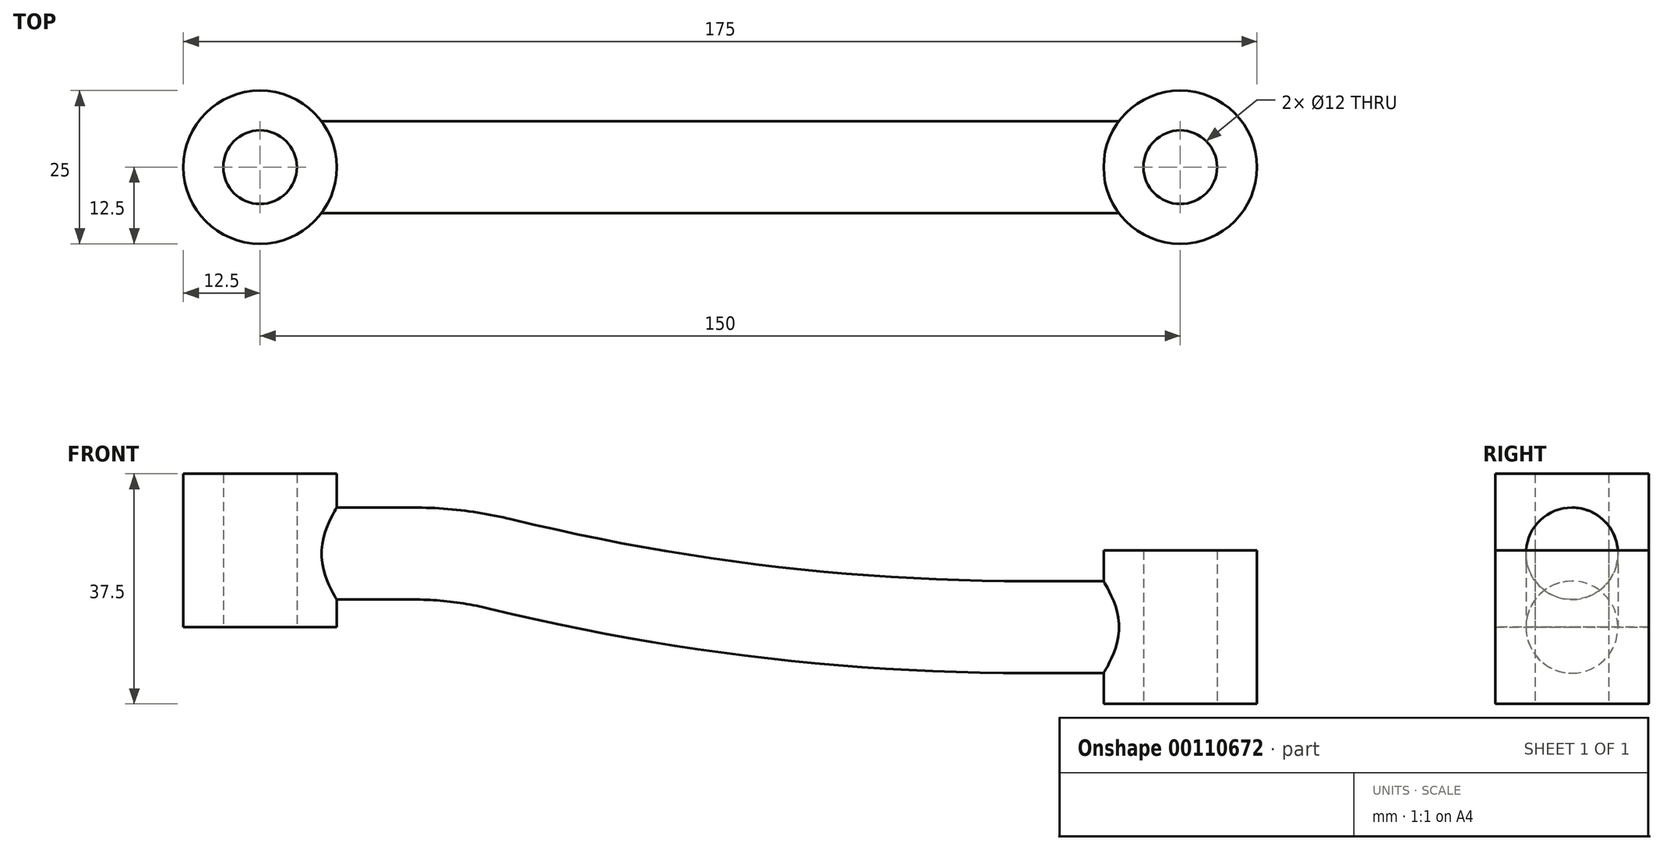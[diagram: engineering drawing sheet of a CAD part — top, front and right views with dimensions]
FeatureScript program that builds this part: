
annotation { "Feature Type Name" : "Feature", "Feature Type Description" : "" }
export const myFeature = defineFeature(function(context is Context, id is Id, definition is map)
    precondition{}
    {
        {
            var Q0;
            Q0=qCreatedBy(makeId("Top.planeOp"),FACE);
            var sketch = newSketch(context, id + "F0", { "sketchPlane" : qUnion([Q0])});
            skCircle(sketch, "E0", {"center": v(0, 0) * mm, "radius": 12.5 * mm});
            skCircle(sketch, "E1", {"center": v(0, 0) * mm, "radius": 6 * mm});
            skCircle(sketch, "E2", {"center": v(150, 0) * mm, "radius": 12.5 * mm});
            skCircle(sketch, "E3", {"center": v(150, 0) * mm, "radius": 6 * mm});
            skLineSegment(sketch, "E4", {"start": v(150, 0) * mm, "end": v(150, 287.37) * mm, "construction": true});
            skSolve(sketch);
        }
        {
            var Q0;
            Q0=makeQuery(id+"F0.imprint","IMPRINT",FACE,{"disambiguationData":[TD([[makeQuery(id+"F0.imprint","IMPRINT",EDGE,{"derivedFrom":sQuery(id+"F0.wireOp",EDGE,"E0")}),1.0]])]});
            extrude(context, id + "F1", {"entities" : qUnion([Q0]), "depth" : 25 * mm});
        }
        {
            var Q0;
            Q0=makeQuery(id+"F0.imprint","IMPRINT",FACE,{"disambiguationData":[TD([[makeQuery(id+"F0.imprint","IMPRINT",EDGE,{"derivedFrom":sQuery(id+"F0.wireOp",EDGE,"E2")}),1.0]])]});
            extrude(context, id + "F2", {"entities" : qUnion([Q0]), "endBound" : BoundingType.SYMMETRIC, "depth" : 25 * mm});
        }
        {
            var Q0;
            Q0=qCreatedBy(makeId("Front.planeOp"),FACE);
            var sketch = newSketch(context, id + "F3", { "sketchPlane" : qUnion([Q0])});
            skLineSegment(sketch, "E5", {"start": v(150, 0) * mm, "end": v(125, 0) * mm});
            skArc(sketch, "E6", {"start": v(39.2, 10.3) * mm, "mid": v(32.15, 11.57) * mm, "end": v(25, 12) * mm});
            skArc(sketch, "E7", {"start": v(39.2, 10.3) * mm, "mid": v(81.79, 2.58) * mm, "end": v(125, 0) * mm});
            skLineSegment(sketch, "E8", {"start": v(25, 12) * mm, "end": v(0, 12) * mm});
            skSolve(sketch);
        }
        {
            var Q0;
            Q0=qCreatedBy(makeId("Right.planeOp"),FACE);
            var sketch = newSketch(context, id + "F4", { "sketchPlane" : qUnion([Q0])});
            skCircle(sketch, "E9", {"center": v(0, 12) * mm, "radius": 7.5 * mm});
            skSolve(sketch);
        }
        {
            var Q0;
            Q0 = qSketchRegion(id + "F4", true);
            var Q1;
            Q1=sQuery(id+"F3.wireOp",EDGE,"E7");
            var Q2;
            Q2=sQuery(id+"F3.wireOp",EDGE,"E6");
            var Q3;
            Q3=sQuery(id+"F3.wireOp",EDGE,"E8");
            var Q4;
            Q4=sQuery(id+"F3.wireOp",EDGE,"E5");
            sweep(context, id + "F5", {"operationType" : NewBodyOperationType.ADD, "profiles" : qUnion([Q0]), "path" : qUnion([Q1, Q2, Q3, Q4])});
        }
        {
            var Q0;
            Q0=makeQuery(id+"F0.imprint","IMPRINT",FACE,{"disambiguationData":[TD([[makeQuery(id+"F0.imprint","IMPRINT",EDGE,{"derivedFrom":sQuery(id+"F0.wireOp",EDGE,"E1")}),1.0]])]});
            var Q1;
            Q1=makeQuery(id+"F0.imprint","IMPRINT",FACE,{"disambiguationData":[TD([[makeQuery(id+"F0.imprint","IMPRINT",EDGE,{"derivedFrom":sQuery(id+"F0.wireOp",EDGE,"E3")}),1.0]])]});
            extrude(context, id + "F6", {"entities" : qUnion([Q0, Q1]), "operationType" : NewBodyOperationType.REMOVE, "endBound" : BoundingType.SYMMETRIC, "depth" : 50 * mm});
        }
    });
